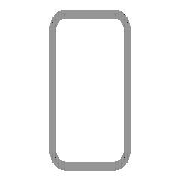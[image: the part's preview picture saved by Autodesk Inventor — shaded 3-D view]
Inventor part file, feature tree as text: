
AUTODESK INVENTOR PART (.ipt)
format: ipt  version: 2025 (Build 290162010, 162A)  size: 129,024 bytes
history: native  units: mm (DEFAULTED — no unit token found)
features: other x3, sketch x1, plane x1
ambient origin geometry x8: Origin, YZ Plane, XZ Plane, XY Plane, X Axis, Y Axis, Z Axis, Center Point
bodies: Solid1 (feature_tree), Body (feature_tree)
feature tree (5):
  other  "Driven Length"
  other  "Start plane"
  other  "End plane"
  sketch  "Sketch3"  dims[d3=691.0mm d4=0.0mm d7=6.0mm d9=40.0mm d11=60.0mm d12=3.0mm d13=-0.0mm d14=691.0mm d15=20.0mm d16=30.0mm d17=90.0deg d18=691.0mm]
  plane  "Work Plane3"
